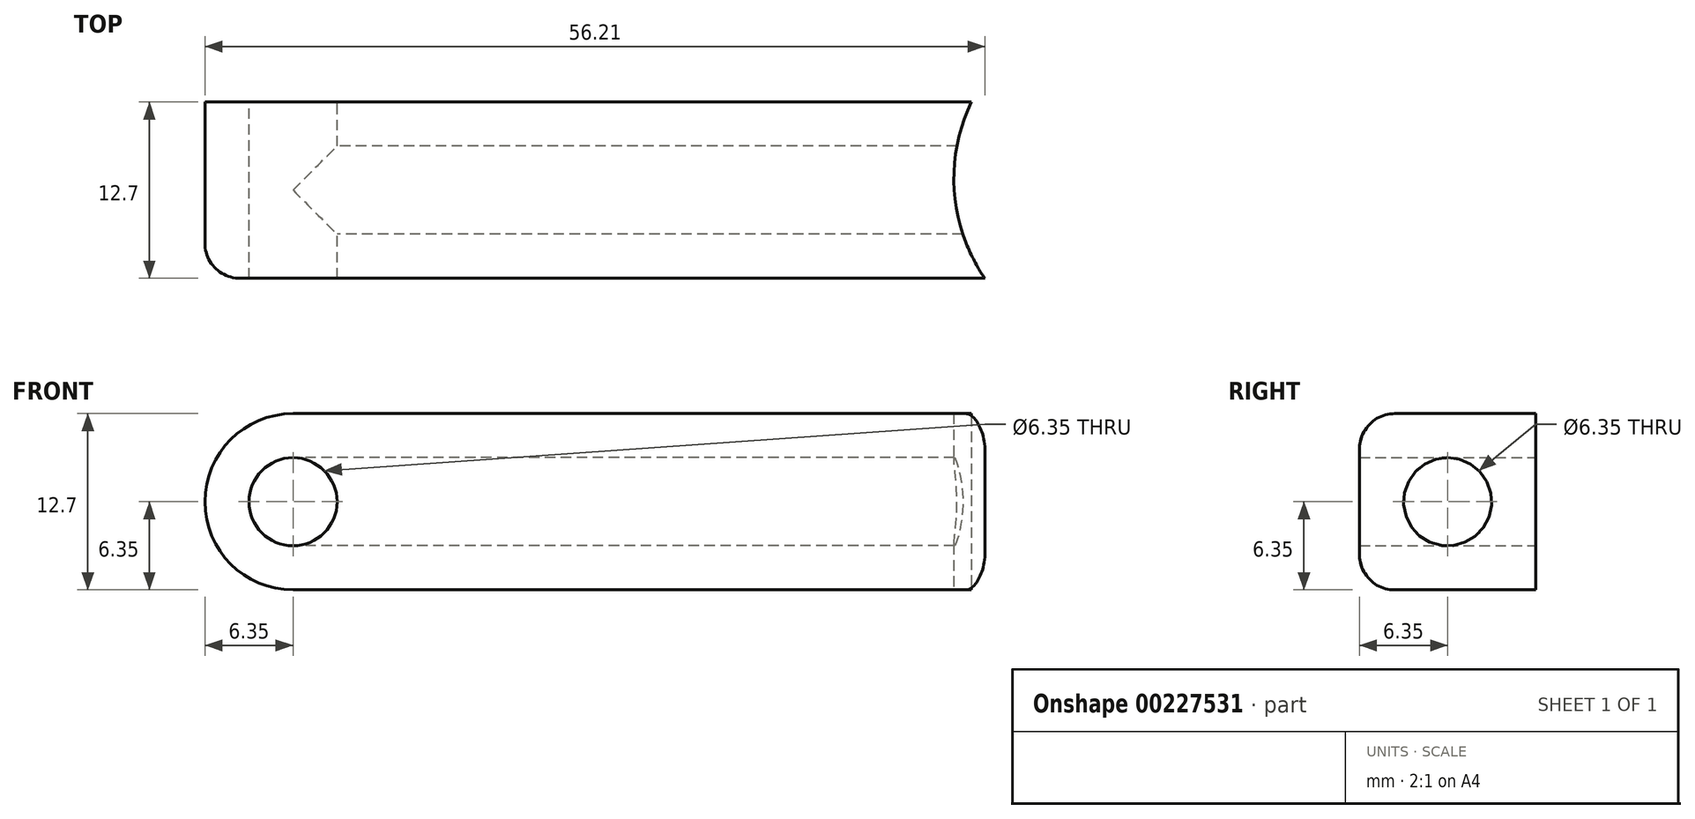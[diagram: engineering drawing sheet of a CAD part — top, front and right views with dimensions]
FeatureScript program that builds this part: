
annotation { "Feature Type Name" : "Feature", "Feature Type Description" : "" }
export const myFeature = defineFeature(function(context is Context, id is Id, definition is map)
    precondition{}
    {
        {
            var Q0;
            Q0=qCreatedBy(makeId("Front.planeOp"),FACE);
            var sketch = newSketch(context, id + "F0", { "sketchPlane" : qUnion([Q0])});
            skLineSegment(sketch, "E0", {"start": v(0, 0) * mm, "end": v(-50.8, 0) * mm, "construction": true});
            skCircle(sketch, "E1", {"center": v(-50.8, 0) * mm, "radius": 6.35 * mm});
            skLineSegment(sketch, "E2", {"start": v(-50.8, 0) * mm, "end": v(-50.8, 15.6) * mm, "construction": true});
            skLineSegment(sketch, "E3", {"start": v(-50.8, 6.35) * mm, "end": v(5.14, 6.35) * mm, "construction": true});
            skLineSegment(sketch, "E4", {"start": v(-50.8, 0) * mm, "end": v(-50.8, -10.69) * mm, "construction": true});
            skLineSegment(sketch, "E5", {"start": v(-50.8, -6.35) * mm, "end": v(5.08, -6.35) * mm, "construction": true});
            skLineSegment(sketch, "E6", {"start": v(0, 0) * mm, "end": v(0, 13.86) * mm, "construction": true});
            skLineSegment(sketch, "E7", {"start": v(0, 13.86) * mm, "end": v(0, -14.11) * mm, "construction": true});
            skLineSegment(sketch, "E8.bottom", {"start": v(-50.8, 6.35) * mm, "end": v(0, 6.35) * mm});
            skLineSegment(sketch, "E8.top", {"start": v(-50.8, -6.35) * mm, "end": v(0, -6.35) * mm});
            skLineSegment(sketch, "E8.left", {"start": v(-50.8, 6.35) * mm, "end": v(-50.8, -6.35) * mm});
            skLineSegment(sketch, "E8.right", {"start": v(0, 6.35) * mm, "end": v(0, -6.35) * mm});
            skCircle(sketch, "E9", {"center": v(-50.8, 0) * mm, "radius": 3.18 * mm});
            skSolve(sketch);
        }
        {
            var Q0;
            Q0=qSketchRegion(id+"F0",true);
            extrude(context, id + "F1", {"entities" : qUnion([Q0]), "depth" : 12.7 * mm});
        }
        {
            var Q0;
            Q0=makeQuery(id+"F1.opExtrude","CAP_EDGE",EDGE,{"disambiguationData":[OSD([sQuery(id+"F0.wireOp",EDGE,"E8.top")])],"isStart":false});
            fillet(context, id + "F2", {"entities" : qUnion([Q0]), "radius" : 2.54 * mm, "tangentPropagation" : true, "allowEdgeOverflow" : false});
        }
        {
            var Q0;
            Q0=qCreatedBy(makeId("Right.planeOp"),FACE);
            var sketch = newSketch(context, id + "F3", { "sketchPlane" : qUnion([Q0])});
            skLineSegment(sketch, "E10", {"start": v(0, 0) * mm, "end": v(-6.35, 0) * mm, "construction": true});
            skCircle(sketch, "E11", {"center": v(-6.35, 0) * mm, "radius": 3.18 * mm});
            skSolve(sketch);
        }
        {
            var Q0;
            Q0=makeQuery(id+"F3.imprint","IMPRINT",FACE,{"disambiguationData":[TD([[makeQuery(id+"F3.imprint","IMPRINT",EDGE,{"derivedFrom":sQuery(id+"F3.wireOp",EDGE,"E11")}),1.0]])]});
            extrude(context, id + "F4", {"entities" : qUnion([Q0]), "operationType" : NewBodyOperationType.REMOVE, "endBound" : BoundingType.SYMMETRIC, "depth" : 101.6 * mm});
        }
        {
            var Q0;
            Q0=qCreatedBy(makeId("Top.planeOp"),FACE);
            var sketch = newSketch(context, id + "F5", { "sketchPlane" : qUnion([Q0])});
            skCircle(sketch, "E12", {"center": v(9.52, -5.5) * mm, "radius": 12.7 * mm});
            skSolve(sketch);
        }
        {
            var Q0;
            Q0=qSketchRegion(id+"F5",true);
            extrude(context, id + "F6", {"entities" : qUnion([Q0]), "operationType" : NewBodyOperationType.REMOVE, "endBound" : BoundingType.SYMMETRIC, "depth" : 76.2 * mm});
        }
    });
